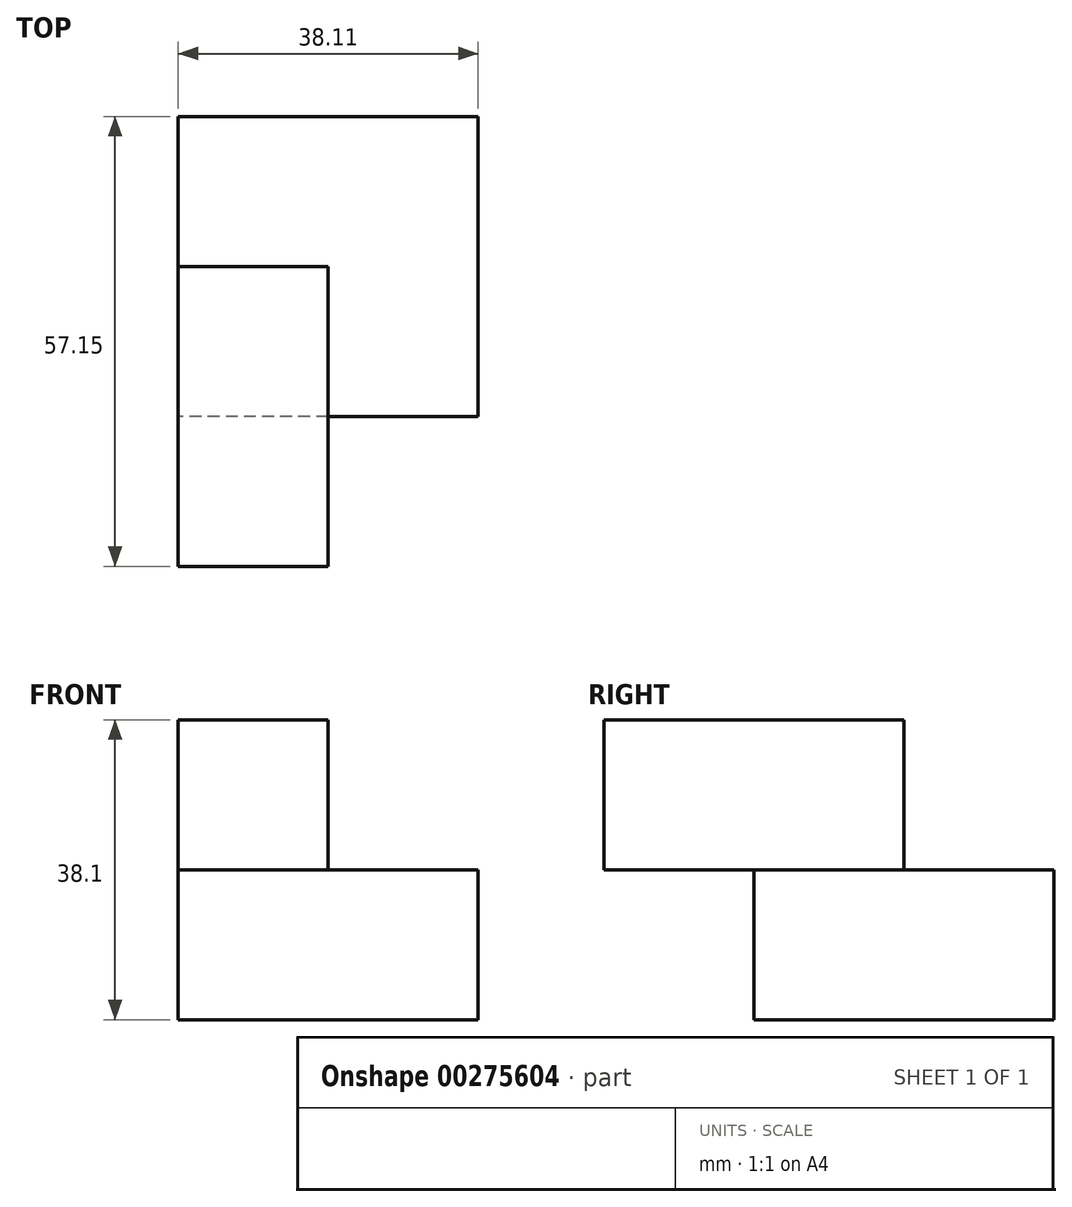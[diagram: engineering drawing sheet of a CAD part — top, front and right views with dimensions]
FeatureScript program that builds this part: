
annotation { "Feature Type Name" : "Feature", "Feature Type Description" : "" }
export const myFeature = defineFeature(function(context is Context, id is Id, definition is map)
    precondition{}
    {
        {
            var Q0;
            Q0=qCreatedBy(makeId("Top.planeOp"),FACE);
            var sketch = newSketch(context, id + "F0", { "sketchPlane" : qUnion([Q0])});
            skLineSegment(sketch, "E0.bottom", {"start": v(-0.95, -7.41) * mm, "end": v(18.1, -7.41) * mm});
            skLineSegment(sketch, "E0.top", {"start": v(-0.95, 11.64) * mm, "end": v(18.1, 11.64) * mm});
            skLineSegment(sketch, "E0.left", {"start": v(-0.95, -7.41) * mm, "end": v(-0.95, 11.64) * mm});
            skLineSegment(sketch, "E0.right", {"start": v(18.1, -7.41) * mm, "end": v(18.1, 11.64) * mm});
            skLineSegment(sketch, "E1.bottom", {"start": v(18.1, 11.64) * mm, "end": v(37.16, 11.64) * mm});
            skLineSegment(sketch, "E1.top", {"start": v(18.1, -7.41) * mm, "end": v(37.16, -7.41) * mm});
            skLineSegment(sketch, "E1.left", {"start": v(18.1, 11.64) * mm, "end": v(18.1, -7.41) * mm});
            skLineSegment(sketch, "E1.right", {"start": v(37.16, 11.64) * mm, "end": v(37.16, -7.41) * mm});
            skLineSegment(sketch, "E2.top", {"start": v(-0.95, -26.46) * mm, "end": v(18.1, -26.46) * mm});
            skLineSegment(sketch, "E2.left", {"start": v(-0.95, -7.41) * mm, "end": v(-0.95, -26.46) * mm});
            skLineSegment(sketch, "E2.right", {"start": v(18.1, -7.41) * mm, "end": v(18.1, -26.46) * mm});
            skLineSegment(sketch, "E3", {"start": v(37.16, -7.41) * mm, "end": v(37.16, -26.46) * mm});
            skLineSegment(sketch, "E4", {"start": v(37.16, -26.46) * mm, "end": v(18.1, -26.46) * mm});
            skSolve(sketch);
        }
        {
            var Q0;
            Q0=makeQuery(id+"F0.imprint","IMPRINT",FACE,{"disambiguationData":[TD([[makeQuery(id+"F0.imprint","IMPRINT",EDGE,{"derivedFrom":sQuery(id+"F0.wireOp",EDGE,"E1.bottom")}),-1.0]])]});
            var Q1;
            Q1=makeQuery(id+"F0.imprint","IMPRINT",FACE,{"disambiguationData":[TD([[makeQuery(id+"F0.imprint","IMPRINT",EDGE,{"derivedFrom":sQuery(id+"F0.wireOp",EDGE,"E0.top")}),-1.0]])]});
            var Q2;
            Q2=makeQuery(id+"F0.imprint","IMPRINT",FACE,{"disambiguationData":[TD([[makeQuery(id+"F0.imprint","IMPRINT",EDGE,{"derivedFrom":sQuery(id+"F0.wireOp",EDGE,"E1.top")}),-1.0]])]});
            extrude(context, id + "F1", {"entities" : qUnion([Q0, Q1, Q2]), "depth" : 19.05 * mm});
        }
        {
            var Q0;
            Q0=makeQuery(id+"F0.imprint","IMPRINT",FACE,{"disambiguationData":[TD([[makeQuery(id+"F0.imprint","IMPRINT",EDGE,{"derivedFrom":sQuery(id+"F0.wireOp",EDGE,"E0.bottom")}),-1.0]])]});
            extrude(context, id + "F2", {"entities" : qUnion([Q0]), "operationType" : NewBodyOperationType.ADD, "depth" : 38.1 * mm});
        }
        {
            var Q0;
            Q0=makeQuery(id+"F2.boolean.opBoolean","MERGE",FACE,{"derivedFrom":[makeQuery(id+"F1.opExtrude","SWEPT_FACE",FACE,{"disambiguationData":[OSD([sQuery(id+"F0.wireOp",EDGE,"E4")])]}),makeQuery(id+"F2.opExtrude","SWEPT_FACE",FACE,{"disambiguationData":[OSD([sQuery(id+"F0.wireOp",EDGE,"E2.top")])]})]});
            var sketch = newSketch(context, id + "F3", { "sketchPlane" : qUnion([Q0])});
            skLineSegment(sketch, "E5", {"start": v(18.1, 19.05) * mm, "end": v(-0.95, 19.05) * mm});
            skLineSegment(sketch, "E6", {"start": v(-0.95, 19.05) * mm, "end": v(-0.95, 38.1) * mm});
            skLineSegment(sketch, "E7", {"start": v(-0.95, 38.1) * mm, "end": v(18.1, 38.1) * mm});
            skLineSegment(sketch, "E8", {"start": v(18.1, 38.1) * mm, "end": v(18.1, 19.05) * mm});
            skSolve(sketch);
        }
        {
            var Q0;
            Q0=makeQuery(id+"F3.imprint","IMPRINT",FACE,{"disambiguationData":[TD([[makeQuery(id+"F3.imprint","IMPRINT",EDGE,{"derivedFrom":sQuery(id+"F3.wireOp",EDGE,"E5")}),-1.0]])]});
            extrude(context, id + "F4", {"entities" : qUnion([Q0]), "operationType" : NewBodyOperationType.ADD, "depth" : 19.05 * mm});
        }
    });
